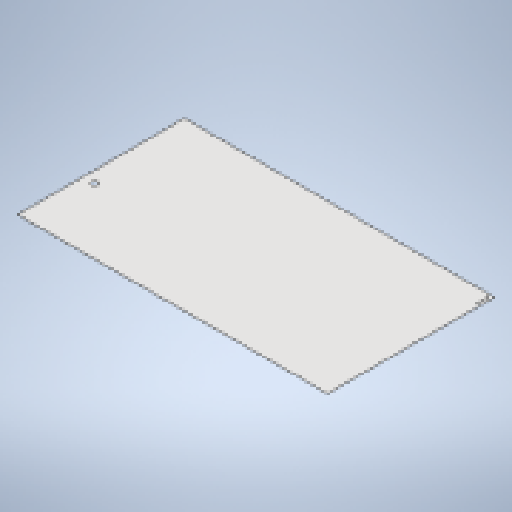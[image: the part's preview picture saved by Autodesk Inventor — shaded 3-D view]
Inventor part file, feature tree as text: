
AUTODESK INVENTOR PART (.ipt)
format: ipt  version: 2025 (Build 290162010, 162A)  size: 235,008 bytes
history: native  units: mm
features: other x3, sketch x3, sheet_metal_op x1, extrude x1
ambient origin geometry x8: Origin, YZ Plane, XZ Plane, XY Plane, X Axis, Y Axis, Z Axis, Center Point
bodies: Solid1 (feature_tree)
feature tree (8):
  sheet_metal_op  "Face1"
  other  "Mark1"
  extrude  "Extrusion2"  Depth=1479.0mm
  sketch  "Sketch1"  dims[d0=2748.0mm d1=1479.0mm]
  other  "Plate1"
  sketch  "Sketch5"  dims[d2=3.0mm]
  sketch  "Sketch6"  dims[d26=200.0mm d27=15.0mm d28=25.0mm d29=25.0mm d30=50.0mm d31=900.0mm d32=100.0mm d33=10.0mm d34=0.0mm]
  other  "Definition1"
